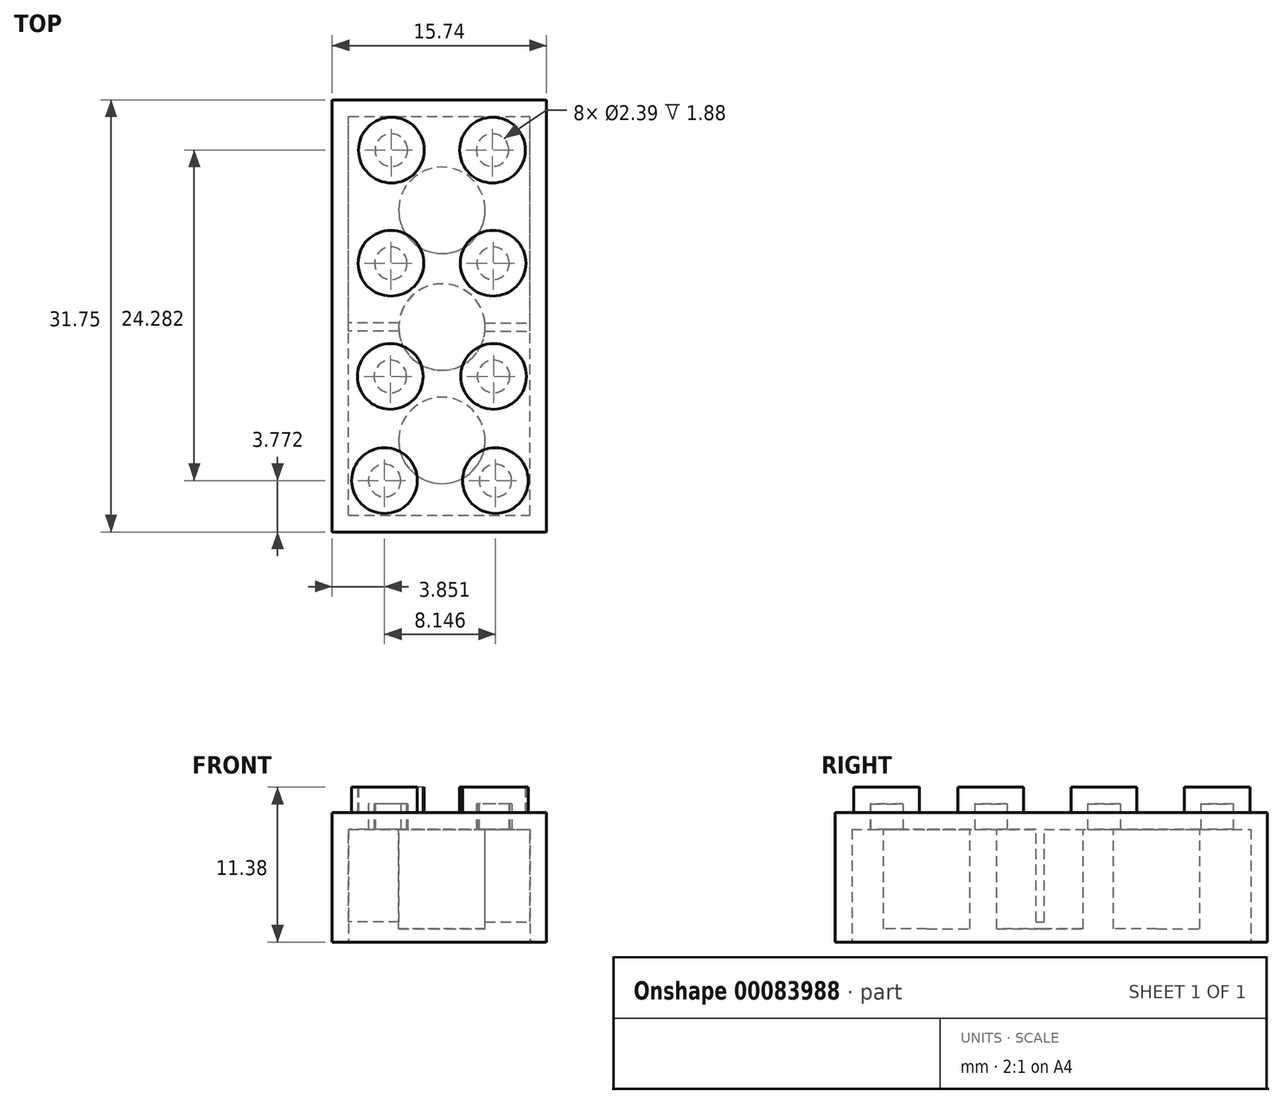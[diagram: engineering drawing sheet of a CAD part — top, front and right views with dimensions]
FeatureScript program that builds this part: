
annotation { "Feature Type Name" : "Feature", "Feature Type Description" : "" }
export const myFeature = defineFeature(function(context is Context, id is Id, definition is map)
    precondition{}
    {
        {
            var Q0;
            Q0=qCreatedBy(makeId("Front.planeOp"),FACE);
            var sketch = newSketch(context, id + "F0", { "sketchPlane" : qUnion([Q0])});
            skLineSegment(sketch, "E0.bottom", {"start": v(-8.07, 5.08) * mm, "end": v(7.67, 5.08) * mm});
            skLineSegment(sketch, "E0.top", {"start": v(-8.07, -4.42) * mm, "end": v(7.67, -4.42) * mm});
            skLineSegment(sketch, "E0.left", {"start": v(-8.07, 5.08) * mm, "end": v(-8.07, -4.42) * mm});
            skLineSegment(sketch, "E0.right", {"start": v(7.67, 5.08) * mm, "end": v(7.67, -4.42) * mm});
            skSolve(sketch);
        }
        {
            var Q0;
            Q0 = qSketchRegion(id + "F0", true);
            extrude(context, id + "F1", {"entities" : qUnion([Q0]), "depth" : 31.75 * mm});
        }
        {
            var Q0;
            Q0=makeQuery(id+"F1.opExtrude","SWEPT_FACE",FACE,{"disambiguationData":[OSD([sQuery(id+"F0.wireOp",EDGE,"E0.bottom")])]});
            var sketch = newSketch(context, id + "F2", { "sketchPlane" : qUnion([Q0])});
            skCircle(sketch, "E1", {"center": v(3.93, -27.98) * mm, "radius": 2.41 * mm});
            skCircle(sketch, "E2.1.0.0", {"center": v(-4.22, -27.98) * mm, "radius": 2.41 * mm});
            skLineSegment(sketch, "E2.direction1", {"start": v(3.93, -27.98) * mm, "end": v(-4.22, -27.98) * mm, "construction": true});
            skSolve(sketch);
        }
        {
            var Q0;
            Q0=makeQuery(id+"F2.imprint","IMPRINT",FACE,{"disambiguationData":[TD([[makeQuery(id+"F2.imprint","IMPRINT",EDGE,{"derivedFrom":sQuery(id+"F2.wireOp",EDGE,"E1")}),1.0]])]});
            var sketch = newSketch(context, id + "F3", { "sketchPlane" : qUnion([Q0])});
            skLineSegment(sketch, "E3", {"start": v(3.8, -24.96) * mm, "end": v(3.8, -22.78) * mm, "construction": true});
            skCircle(sketch, "E4", {"center": v(3.8, -20.32) * mm, "radius": 2.41 * mm});
            skLineSegment(sketch, "E5.1.0.0", {"start": v(3.75, -16.65) * mm, "end": v(3.75, -14.47) * mm, "construction": true});
            skCircle(sketch, "E5.1.0.1", {"center": v(3.75, -12) * mm, "radius": 2.41 * mm});
            skLineSegment(sketch, "E5.2.0.0", {"start": v(3.72, -8.33) * mm, "end": v(3.72, -6.16) * mm, "construction": true});
            skCircle(sketch, "E5.2.0.1", {"center": v(3.72, -3.7) * mm, "radius": 2.41 * mm});
            skLineSegment(sketch, "E5.direction1", {"start": v(3.8, -24.96) * mm, "end": v(3.75, -16.65) * mm, "construction": true});
            skCircle(sketch, "E6.MirrorC", {"center": v(-3.72, -3.7) * mm, "radius": 2.41 * mm});
            skCircle(sketch, "E7.MirrorC", {"center": v(-3.75, -12) * mm, "radius": 2.41 * mm});
            skCircle(sketch, "E8.MirrorC", {"center": v(-3.8, -20.32) * mm, "radius": 2.41 * mm});
            skSolve(sketch);
        }
        {
            var Q0;
            Q0=makeQuery(id+"F2.imprint","IMPRINT",FACE,{"disambiguationData":[TD([[makeQuery(id+"F2.imprint","IMPRINT",EDGE,{"derivedFrom":sQuery(id+"F2.wireOp",EDGE,"E2.1.0.0")}),1.0]])]});
            var Q1;
            Q1=makeQuery(id+"F2.imprint","IMPRINT",FACE,{"disambiguationData":[TD([[makeQuery(id+"F2.imprint","IMPRINT",EDGE,{"derivedFrom":sQuery(id+"F2.wireOp",EDGE,"E1")}),1.0]])]});
            var Q2;
            Q2=sQuery(id+"F2.wireOp",EDGE,"E1");
            var Q3;
            Q3=sQuery(id+"F2.wireOp",EDGE,"E2.1.0.0");
            extrude(context, id + "F4", {"entities" : qUnion([Q0, Q1]), "operationType" : NewBodyOperationType.ADD, "surfaceEntities" : qUnion([Q2, Q3]), "depth" : 1.88 * mm});
        }
        {
            var Q0;
            Q0 = qSketchRegion(id + "F3", true);
            var Q1;
            Q1=sQuery(id+"F3.wireOp",EDGE,"E6.MirrorC");
            var Q2;
            Q2=sQuery(id+"F3.wireOp",EDGE,"E7.MirrorC");
            var Q3;
            Q3=sQuery(id+"F3.wireOp",EDGE,"E8.MirrorC");
            var Q4;
            Q4=sQuery(id+"F2.wireOp",EDGE,"E2.1.0.0");
            var Q5;
            Q5=sQuery(id+"F2.wireOp",EDGE,"E1");
            var Q6;
            Q6=sQuery(id+"F3.wireOp",EDGE,"E4");
            var Q7;
            Q7=sQuery(id+"F3.wireOp",EDGE,"E5.1.0.1");
            var Q8;
            Q8=sQuery(id+"F3.wireOp",EDGE,"E5.2.0.1");
            extrude(context, id + "F5", {"entities" : qUnion([Q0]), "operationType" : NewBodyOperationType.ADD, "surfaceEntities" : qUnion([Q1, Q2, Q3, Q4, Q5, Q6, Q7, Q8]), "depth" : 1.88 * mm});
        }
        {
            var Q0;
            Q0=makeQuery(id+"F1.opExtrude","SWEPT_FACE",FACE,{"disambiguationData":[OSD([sQuery(id+"F0.wireOp",EDGE,"E0.top")])]});
            shell(context, id + "F6", {"entities" : qUnion([Q0]), "thickness" : 1.22 * mm});
        }
        {
            var Q0;
            Q0=makeQuery(id+"F6.opShell","OFFSET_FACE",FACE,{"disambiguationData":[OSD([sQuery(id+"F0.wireOp",EDGE,"E0.bottom")])]});
            var sketch = newSketch(context, id + "F7", { "sketchPlane" : qUnion([Q0])});
            skCircle(sketch, "E9", {"center": v(0, 25.02) * mm, "radius": 3.18 * mm});
            skCircle(sketch, "E10", {"center": v(0, 16.7) * mm, "radius": 3.18 * mm});
            skCircle(sketch, "E11", {"center": v(0, 8.12) * mm, "radius": 3.18 * mm});
            skLineSegment(sketch, "E12", {"start": v(3.18, 16.7) * mm, "end": v(6.45, 16.7) * mm});
            skLineSegment(sketch, "E13", {"start": v(-3.18, 16.7) * mm, "end": v(-6.85, 16.7) * mm});
            skSolve(sketch);
        }
        {
            var Q0;
            Q0=makeQuery(id+"F7.imprint","IMPRINT",FACE,{"disambiguationData":[TD([[makeQuery(id+"F7.imprint","IMPRINT",EDGE,{"derivedFrom":sQuery(id+"F7.wireOp",EDGE,"E11")}),1.0]])]});
            var Q1;
            Q1=sQuery(id+"F7.wireOp",EDGE,"E11");
            extrude(context, id + "F8", {"entities" : qUnion([Q0]), "operationType" : NewBodyOperationType.ADD, "surfaceEntities" : qUnion([Q1]), "depth" : 7.32 * mm});
        }
        {
            var Q0;
            Q0=makeQuery(id+"F7.imprint","IMPRINT",FACE,{"disambiguationData":[TD([[makeQuery(id+"F7.imprint","IMPRINT",EDGE,{"derivedFrom":sQuery(id+"F7.wireOp",EDGE,"E9")}),1.0]])]});
            var Q1;
            Q1=sQuery(id+"F7.wireOp",EDGE,"E9");
            extrude(context, id + "F9", {"entities" : qUnion([Q0]), "operationType" : NewBodyOperationType.ADD, "surfaceEntities" : qUnion([Q1]), "depth" : 7.32 * mm});
        }
        {
            var Q0;
            {var subQ0=sQuery(id+"F7.wireOp",EDGE,"E10");var subQ1=makeQuery(id+"F7.imprint","INTERSECT",VERTEX,{"derivedFrom":[subQ0,sQuery(id+"F7.wireOp",EDGE,"Wq6QDWjZ-qPOK-o6nQ-V1hH-HIMJpwt8gVtT.bottom"),sQuery(id+"F7.wireOp",EDGE,"Wq6QDWjZ-qPOK-o6nQ-V1hH-HIMJpwt8gVtT.left")]});Q0=makeQuery(id+"F7.imprint","IMPRINT",FACE,{"disambiguationData":[TD([[makeQuery(id+"F7.imprint","IMPRINT",EDGE,{"disambiguationData":[TD([[subQ1,-1.0]])],"derivedFrom":subQ0}),1.0]])]});}
            extrude(context, id + "F10", {"entities" : qUnion([Q0]), "operationType" : NewBodyOperationType.ADD, "depth" : 7.32 * mm});
        }
        {
            var Q0;
            Q0=makeQuery(id+"F6.opShell","OFFSET_FACE",FACE,{"disambiguationData":[OSD([sQuery(id+"F0.wireOp",EDGE,"E0.bottom")])]});
            var sketch = newSketch(context, id + "F11", { "sketchPlane" : qUnion([Q0])});
            skLineSegment(sketch, "E14.bottom", {"start": v(-3.16, 17) * mm, "end": v(-6.85, 17) * mm});
            skLineSegment(sketch, "E14.top", {"start": v(-3.16, 16.4) * mm, "end": v(-6.85, 16.4) * mm});
            skLineSegment(sketch, "E14.left", {"start": v(-3.16, 17) * mm, "end": v(-3.16, 16.4) * mm});
            skLineSegment(sketch, "E14.right", {"start": v(-6.85, 17) * mm, "end": v(-6.85, 16.4) * mm});
            skLineSegment(sketch, "E15.bottom", {"start": v(3.16, 17) * mm, "end": v(6.45, 17) * mm});
            skLineSegment(sketch, "E15.top", {"start": v(3.16, 16.4) * mm, "end": v(6.45, 16.4) * mm});
            skLineSegment(sketch, "E15.left", {"start": v(3.16, 17) * mm, "end": v(3.16, 16.4) * mm});
            skLineSegment(sketch, "E15.right", {"start": v(6.45, 17) * mm, "end": v(6.45, 16.4) * mm});
            skSolve(sketch);
        }
        {
            var Q0;
            {var subQ0=sQuery(id+"F11.wireOp",EDGE,"E14.bottom");Q0=makeQuery(id+"F11.imprint","IMPRINT",FACE,{"disambiguationData":[TD([[makeQuery(id+"F11.imprint","IMPRINT",EDGE,{"derivedFrom":subQ0}),1.0]])]});}
            var Q1;
            {var subQ0=sQuery(id+"F11.wireOp",EDGE,"E15.bottom");Q1=makeQuery(id+"F11.imprint","IMPRINT",FACE,{"disambiguationData":[TD([[makeQuery(id+"F11.imprint","IMPRINT",EDGE,{"derivedFrom":subQ0}),-1.0]])]});}
            var Q2;
            Q2=sQuery(id+"F11.wireOp",EDGE,"E14.bottom");
            var Q3;
            Q3=sQuery(id+"F11.wireOp",EDGE,"E14.right");
            var Q4;
            Q4=sQuery(id+"F11.wireOp",EDGE,"E14.top");
            var Q5;
            Q5=sQuery(id+"F11.wireOp",EDGE,"E14.left");
            var Q6;
            Q6=sQuery(id+"F11.wireOp",EDGE,"E15.left");
            var Q7;
            Q7=sQuery(id+"F11.wireOp",EDGE,"E15.top");
            var Q8;
            Q8=sQuery(id+"F11.wireOp",EDGE,"E15.bottom");
            var Q9;
            Q9=sQuery(id+"F11.wireOp",EDGE,"E15.right");
            extrude(context, id + "F12", {"entities" : qUnion([Q0, Q1]), "operationType" : NewBodyOperationType.ADD, "surfaceEntities" : qUnion([Q2, Q3, Q4, Q5, Q6, Q7, Q8, Q9]), "depth" : 6.8 * mm});
        }
    });
